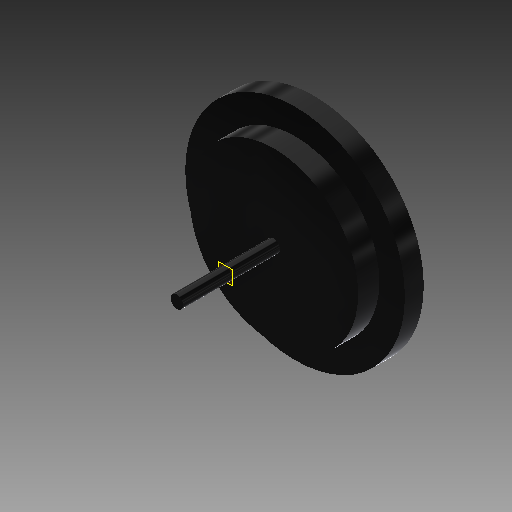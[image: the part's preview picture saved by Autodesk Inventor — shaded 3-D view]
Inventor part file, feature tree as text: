
AUTODESK INVENTOR PART (.ipt)
format: ipt  version: 2017 (Build 210142000, 142)  size: 169,984 bytes
history: native  units: mm
features: extrude x5, sketch x5, fillet x2, plane x1
ambient origin geometry x8: Origin, YZ Plane, XZ Plane, XY Plane, X Axis, Y Axis, Z Axis, Center Point
bodies: Solid1 (feature_tree)
feature tree (13):
  extrude  "Extrusion1"  Depth=12.0mm TaperAngle=0.0deg
  extrude  "Extrusion2"  Depth=19.0mm TaperAngle=0.0deg
  plane  "Work Plane1"
  extrude  "Extrusion6"  Depth=43.0mm
  extrude  "Extrusion9"  Depth=5.0mm TaperAngle=0.0deg
  extrude  "Extrusion10"  Depth=3.0mm TaperAngle=0.0deg
  fillet  "Fillet1"  Radius=2.0mm
  fillet  "Fillet2"  Radius=2.0mm
  sketch  "Sketch2"  dims[d0=33.0mm d1=12.0mm d2=0.0mm]
  sketch  "Sketch3"  dims[d3=2.5mm d4=19.0mm d5=0.0mm]
  sketch  "Sketch7"  dims[d6=-9.5mm d19=43.0mm]
  sketch  "Sketch12"  dims[d20=3.7mm d21=0.0mm d31=5.0mm d32=0.0mm]
  sketch  "Sketch13"  dims[d33=2.0mm d34=3.0mm d35=0.0mm d36=2.0mm d37=2.0mm]
